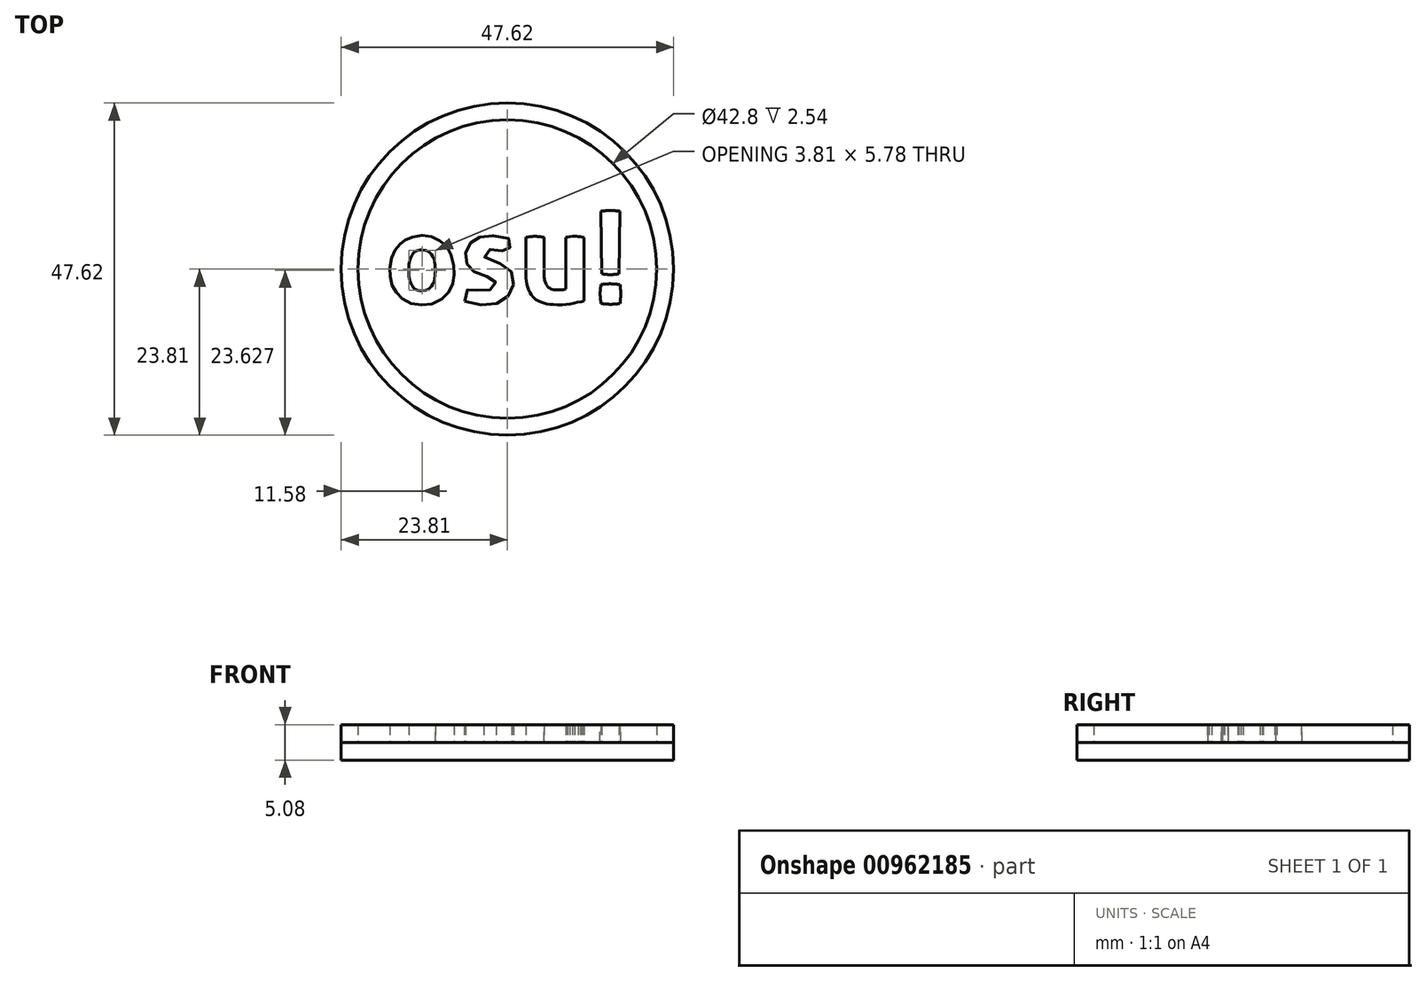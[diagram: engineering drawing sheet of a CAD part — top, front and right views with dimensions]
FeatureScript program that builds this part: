
annotation { "Feature Type Name" : "Feature", "Feature Type Description" : "" }
export const myFeature = defineFeature(function(context is Context, id is Id, definition is map)
    precondition{}
    {
        {
            var Q0;
            Q0=qCreatedBy(makeId("Top.planeOp"),FACE);
            var sketch = newSketch(context, id + "F0", { "sketchPlane" : qUnion([Q0])});
            skCircle(sketch, "E0", {"center": v(0, 0) * mm, "radius": 23.81 * mm});
            skCircle(sketch, "E1.0", {"center": v(0, 0) * mm, "radius": 21.4 * mm});
            skFitSpline(sketch, "E2", {"points": [v(-12.19, 4.8) * mm, v(-11.22, 4.72) * mm, v(-10.21, 4.36) * mm, v(-9.48, 3.92) * mm, v(-8.76, 3.35) * mm, v(-8.2, 2.5) * mm, v(-7.83, 1.1) * mm, v(-7.63, 0) * mm, v(-7.67, -1.09) * mm, v(-7.79, -1.93) * mm, v(-8.2, -2.94) * mm, v(-8.68, -3.67) * mm, v(-9.8, -4.56) * mm, v(-11.06, -5.08) * mm, v(-12.27, -5.16) * mm, v(-13.56, -5.04) * mm, v(-14.77, -4.48) * mm, v(-15.46, -3.87) * mm, v(-15.98, -3.23) * mm, v(-16.38, -2.54) * mm, v(-16.7, -1.65) * mm, v(-16.79, -0.8) * mm, v(-16.83, 0) * mm, v(-16.67, 1.33) * mm, v(-16.34, 2.14) * mm, v(-15.98, 2.9) * mm, v(-15.5, 3.47) * mm, v(-15.19, 3.79) * mm, v(-14.82, 4.06) * mm, v(-14.12, 4.44) * mm, v(-13.4, 4.64) * mm, v(-12.19, 4.8) * mm]});
            skFitSpline(sketch, "E3", {"points": [v(-6.11, -4.64) * mm, v(-6.08, -4.07) * mm, v(-6, -3.67) * mm, v(-5.8, -3.16) * mm, v(-5.6, -2.67) * mm, v(-5.23, -2.81) * mm, v(-4.71, -2.96) * mm, v(-4.12, -3.07) * mm, v(-3.63, -3.13) * mm, v(-2.8, -3.07) * mm, v(-2.15, -2.84) * mm, v(-1.75, -2.5) * mm, v(-1.63, -2.27) * mm, v(-1.66, -1.87) * mm, v(-1.83, -1.56) * mm, v(-2.2, -1.3) * mm, v(-2.72, -1.13) * mm, v(-3.2, -0.96) * mm, v(-4.09, -0.7) * mm, v(-4.69, -0.42) * mm, v(-5.03, -0.22) * mm, v(-5.31, 0) * mm, v(-5.6, 0.32) * mm, v(-5.83, 0.87) * mm, v(-5.94, 1.35) * mm, v(-6, 1.72) * mm, v(-6, 2.15) * mm, v(-5.88, 2.6) * mm, v(-5.71, 2.98) * mm, v(-5.51, 3.43) * mm, v(-5.14, 3.92) * mm, v(-4.77, 4.15) * mm, v(-4.34, 4.38) * mm, v(-3.92, 4.58) * mm, v(-3.32, 4.72) * mm, v(-2.69, 4.8) * mm, v(-1.89, 4.78) * mm, v(-0.84, 4.67) * mm, v(0, 4.46) * mm, v(0.57, 4.25) * mm, v(0.53, 3.8) * mm, v(0.42, 3.28) * mm, v(0.3, 2.9) * mm, v(0, 2.41) * mm, v(-0.34, 2.5) * mm, v(-0.7, 2.61) * mm, v(-1.35, 2.8) * mm, v(-1.88, 2.82) * mm, v(-2.35, 2.84) * mm, v(-2.89, 2.74) * mm, v(-3.2, 2.52) * mm, v(-3.35, 2.07) * mm, v(-3.09, 1.44) * mm, v(-2.72, 1.27) * mm, v(-0.98, 0.72) * mm, v(-0.25, 0.37) * mm, v(0.26, 0) * mm, v(0.65, -0.59) * mm, v(0.82, -1.27) * mm, v(0.9, -1.75) * mm, v(0.85, -2.56) * mm, v(0.68, -3.13) * mm, v(0.36, -3.6) * mm, v(0, -4.01) * mm, v(-0.48, -4.43) * mm, v(-1.2, -4.81) * mm, v(-2.3, -5.07) * mm, v(-3.09, -5.13) * mm, v(-3.98, -5.12) * mm, v(-5.28, -4.92) * mm, v(-6.11, -4.64) * mm]});
            skFitSpline(sketch, "E4", {"points": [v(2.64, 4.58) * mm, v(2.93, 4.6) * mm, v(3.14, 4.63) * mm, v(3.6, 4.67) * mm, v(4.26, 4.68) * mm, v(4.71, 4.63) * mm, v(5.09, 4.58) * mm, v(5.26, 4.54) * mm], "startDerivative": vector(2.37, 0.1) * mm, "endDerivative": vector(1.54, -0.42) * mm});
            skLineSegment(sketch, "E5", {"start": v(5.26, 4.54) * mm, "end": v(5.26, -0.8) * mm});
            skLineSegment(sketch, "E6", {"start": v(2.64, 4.58) * mm, "end": v(2.64, -0.83) * mm});
            skFitSpline(sketch, "E7", {"points": [v(5.26, -0.8) * mm, v(5.27, -1.09) * mm, v(5.3, -1.34) * mm, v(5.34, -1.54) * mm, v(5.39, -1.78) * mm, v(5.46, -1.96) * mm, v(5.53, -2.1) * mm, v(5.64, -2.33) * mm, v(5.75, -2.46) * mm, v(5.9, -2.6) * mm, v(6.1, -2.75) * mm, v(6.27, -2.86) * mm, v(6.58, -2.95) * mm, v(6.74, -2.97) * mm, v(7.03, -2.99) * mm, v(7.58, -2.97) * mm, v(7.83, -2.97) * mm, v(8.1, -2.93) * mm, v(8.37, -2.87) * mm], "startDerivative": vector(-0.18, -4.92) * mm, "endDerivative": vector(5.8, 1.77) * mm});
            skFitSpline(sketch, "E8", {"points": [v(2.64, -0.83) * mm, v(2.65, -1.1) * mm, v(2.68, -1.33) * mm, v(2.73, -1.72) * mm, v(2.77, -2.06) * mm, v(2.82, -2.33) * mm, v(2.9, -2.59) * mm, v(3, -2.85) * mm, v(3.1, -3.13) * mm, v(3.23, -3.35) * mm, v(3.38, -3.6) * mm, v(3.52, -3.8) * mm, v(3.72, -4.05) * mm, v(4, -4.3) * mm, v(4.24, -4.46) * mm, v(4.47, -4.59) * mm, v(4.8, -4.75) * mm, v(5.08, -4.86) * mm, v(5.28, -4.9) * mm, v(5.54, -4.98) * mm, v(5.81, -5.01) * mm, v(6.14, -5.05) * mm, v(6.5, -5.08) * mm, v(6.78, -5.1) * mm, v(7.74, -5.13) * mm, v(8.09, -5.08) * mm, v(8.71, -5.02) * mm, v(9.15, -4.97) * mm, v(9.63, -4.88) * mm, v(9.96, -4.78) * mm, v(10.43, -4.68) * mm, v(10.75, -4.62) * mm, v(10.96, -4.56) * mm], "startDerivative": vector(0.02, -9.82) * mm, "endDerivative": vector(8.04, 2.76) * mm});
            skLineSegment(sketch, "E9", {"start": v(10.96, -4.56) * mm, "end": v(10.96, 4.51) * mm});
            skLineSegment(sketch, "E10", {"start": v(8.37, -2.87) * mm, "end": v(8.37, 4.51) * mm});
            skLineSegment(sketch, "E11", {"start": v(8.37, 4.51) * mm, "end": v(8.5, 4.56) * mm});
            skLineSegment(sketch, "E12", {"start": v(8.5, 4.56) * mm, "end": v(8.64, 4.6) * mm});
            skLineSegment(sketch, "E13", {"start": v(8.64, 4.6) * mm, "end": v(8.92, 4.65) * mm});
            skLineSegment(sketch, "E14", {"start": v(9.3, 4.7) * mm, "end": v(8.92, 4.65) * mm});
            skLineSegment(sketch, "E15", {"start": v(9.3, 4.7) * mm, "end": v(9.64, 4.7) * mm});
            skLineSegment(sketch, "E16", {"start": v(9.64, 4.7) * mm, "end": v(9.91, 4.68) * mm});
            skLineSegment(sketch, "E17", {"start": v(9.91, 4.68) * mm, "end": v(10.18, 4.65) * mm});
            skLineSegment(sketch, "E18", {"start": v(10.18, 4.65) * mm, "end": v(10.45, 4.62) * mm});
            skLineSegment(sketch, "E19", {"start": v(10.45, 4.62) * mm, "end": v(10.74, 4.57) * mm});
            skLineSegment(sketch, "E20", {"start": v(10.74, 4.57) * mm, "end": v(10.96, 4.51) * mm});
            skFitSpline(sketch, "E21", {"points": [v(-14.13, 0) * mm, v(-14.1, 0.41) * mm, v(-14.05, 0.89) * mm, v(-13.95, 1.37) * mm, v(-13.77, 1.81) * mm, v(-13.63, 2.05) * mm, v(-13.47, 2.3) * mm, v(-13.2, 2.5) * mm, v(-12.93, 2.65) * mm, v(-12.66, 2.7) * mm, v(-11.93, 2.72) * mm, v(-11.34, 2.55) * mm, v(-10.94, 2.22) * mm, v(-10.58, 1.64) * mm, v(-10.4, 0.98) * mm, v(-10.33, 0.22) * mm, v(-10.33, 0) * mm], "startDerivative": vector(0.3, 6.9) * mm, "endDerivative": vector(-0.47, -4.32) * mm});
            skFitSpline(sketch, "E22.MirrorCS", {"points": [v(-14.13, -0.37) * mm, v(-14.1, -0.78) * mm, v(-14.05, -1.25) * mm, v(-13.95, -1.74) * mm, v(-13.77, -2.18) * mm, v(-13.63, -2.42) * mm, v(-13.47, -2.67) * mm, v(-13.2, -2.87) * mm, v(-12.93, -3.02) * mm, v(-12.66, -3.07) * mm, v(-11.93, -3.09) * mm, v(-11.34, -2.92) * mm, v(-10.94, -2.59) * mm, v(-10.58, -2) * mm, v(-10.4, -1.35) * mm, v(-10.33, -0.58) * mm, v(-10.33, -0.37) * mm], "startDerivative": vector(0.3, -6.9) * mm, "endDerivative": vector(-0.47, 4.32) * mm});
            skFitSpline(sketch, "E23", {"points": [v(-14.13, -0.37) * mm, v(-14.13, -0.2) * mm, v(-14.13, 0) * mm], "startDerivative": vector(0, 0.35) * mm, "endDerivative": vector(0, 0.38) * mm});
            skFitSpline(sketch, "E24", {"points": [v(-10.33, -0.37) * mm, v(-10.33, -0.2) * mm, v(-10.33, 0) * mm], "startDerivative": vector(0, 0.35) * mm, "endDerivative": vector(0, 0.38) * mm});
            skFitSpline(sketch, "E25", {"points": [v(13.4, -2.2) * mm, v(14.72, -2.12) * mm, v(16.14, -2.22) * mm], "startDerivative": vector(2.66, 0.28) * mm, "endDerivative": vector(2.8, -0.31) * mm});
            skFitSpline(sketch, "E26", {"points": [v(16.14, -2.22) * mm, v(16.23, -3.5) * mm, v(16.14, -4.94) * mm], "startDerivative": vector(0.3, -2.57) * mm, "endDerivative": vector(-0.29, -2.85) * mm});
            skFitSpline(sketch, "E27", {"points": [v(16.14, -4.94) * mm, v(14.81, -5.04) * mm, v(13.42, -4.94) * mm], "startDerivative": vector(-2.67, -0.33) * mm, "endDerivative": vector(-2.78, 0.32) * mm});
            skFitSpline(sketch, "E28", {"points": [v(13.42, -4.94) * mm, v(13.28, -3.55) * mm, v(13.4, -2.2) * mm], "startDerivative": vector(-0.39, 2.76) * mm, "endDerivative": vector(0.37, 2.7) * mm});
            skFitSpline(sketch, "E29", {"points": [v(13.4, 8.29) * mm, v(14.7, 8.4) * mm, v(16.14, 8.29) * mm], "startDerivative": vector(2.63, 0.33) * mm, "endDerivative": vector(2.84, -0.32) * mm});
            skFitSpline(sketch, "E30", {"points": [v(13.52, -0.69) * mm, v(14.74, -0.8) * mm, v(16, -0.68) * mm], "startDerivative": vector(2.46, -0.35) * mm, "endDerivative": vector(2.5, 0.36) * mm});
            skLineSegment(sketch, "E31", {"start": v(13.4, 8.29) * mm, "end": v(13.52, -0.69) * mm});
            skLineSegment(sketch, "E32", {"start": v(16.14, 8.29) * mm, "end": v(16, -0.68) * mm});
            skSolve(sketch);
        }
        {
            var Q0;
            Q0=makeQuery(id+"F0.imprint","IMPRINT",FACE,{"disambiguationData":[TD([[makeQuery(id+"F0.imprint","IMPRINT",EDGE,{"derivedFrom":sQuery(id+"F0.wireOp",EDGE,"E0")}),1.0]])]});
            var Q1;
            Q1=makeQuery(id+"F0.imprint","IMPRINT",FACE,{"disambiguationData":[TD([[makeQuery(id+"F0.imprint","IMPRINT",EDGE,{"derivedFrom":sQuery(id+"F0.wireOp",EDGE,"E2")}),-1.0]])]});
            var Q2;
            Q2=makeQuery(id+"F0.imprint","IMPRINT",FACE,{"disambiguationData":[TD([[makeQuery(id+"F0.imprint","IMPRINT",EDGE,{"derivedFrom":sQuery(id+"F0.wireOp",EDGE,"E3")}),-1.0]])]});
            var Q3;
            Q3=makeQuery(id+"F0.imprint","IMPRINT",FACE,{"disambiguationData":[TD([[makeQuery(id+"F0.imprint","IMPRINT",EDGE,{"derivedFrom":sQuery(id+"F0.wireOp",EDGE,"E4")}),-1.0]])]});
            var Q4;
            Q4=makeQuery(id+"F0.imprint","IMPRINT",FACE,{"disambiguationData":[TD([[makeQuery(id+"F0.imprint","IMPRINT",EDGE,{"derivedFrom":sQuery(id+"F0.wireOp",EDGE,"E29")}),-1.0]])]});
            var Q5;
            Q5=makeQuery(id+"F0.imprint","IMPRINT",FACE,{"disambiguationData":[TD([[makeQuery(id+"F0.imprint","IMPRINT",EDGE,{"derivedFrom":sQuery(id+"F0.wireOp",EDGE,"E25")}),-1.0]])]});
            extrude(context, id + "F1", {"entities" : qUnion([Q0, Q1, Q2, Q3, Q4, Q5]), "depth" : 2.54 * mm, "offsetDistance" : 25.4 * mm});
        }
        {
            var Q0;
            Q0=qCreatedBy(makeId("Top.planeOp"),FACE);
            var sketch = newSketch(context, id + "F2", { "sketchPlane" : qUnion([Q0])});
            skCircle(sketch, "E33", {"center": v(0, 0) * mm, "radius": 23.81 * mm});
            skSolve(sketch);
        }
        {
            var Q0;
            Q0=makeQuery(id+"F2.imprint","IMPRINT",FACE,{"disambiguationData":[TD([[makeQuery(id+"F2.imprint","IMPRINT",EDGE,{"derivedFrom":sQuery(id+"F2.wireOp",EDGE,"E33")}),1.0]])]});
            extrude(context, id + "F3", {"entities" : qUnion([Q0]), "oppositeDirection" : true, "depth" : 2.54 * mm, "offsetDistance" : 25.4 * mm});
        }
    });
